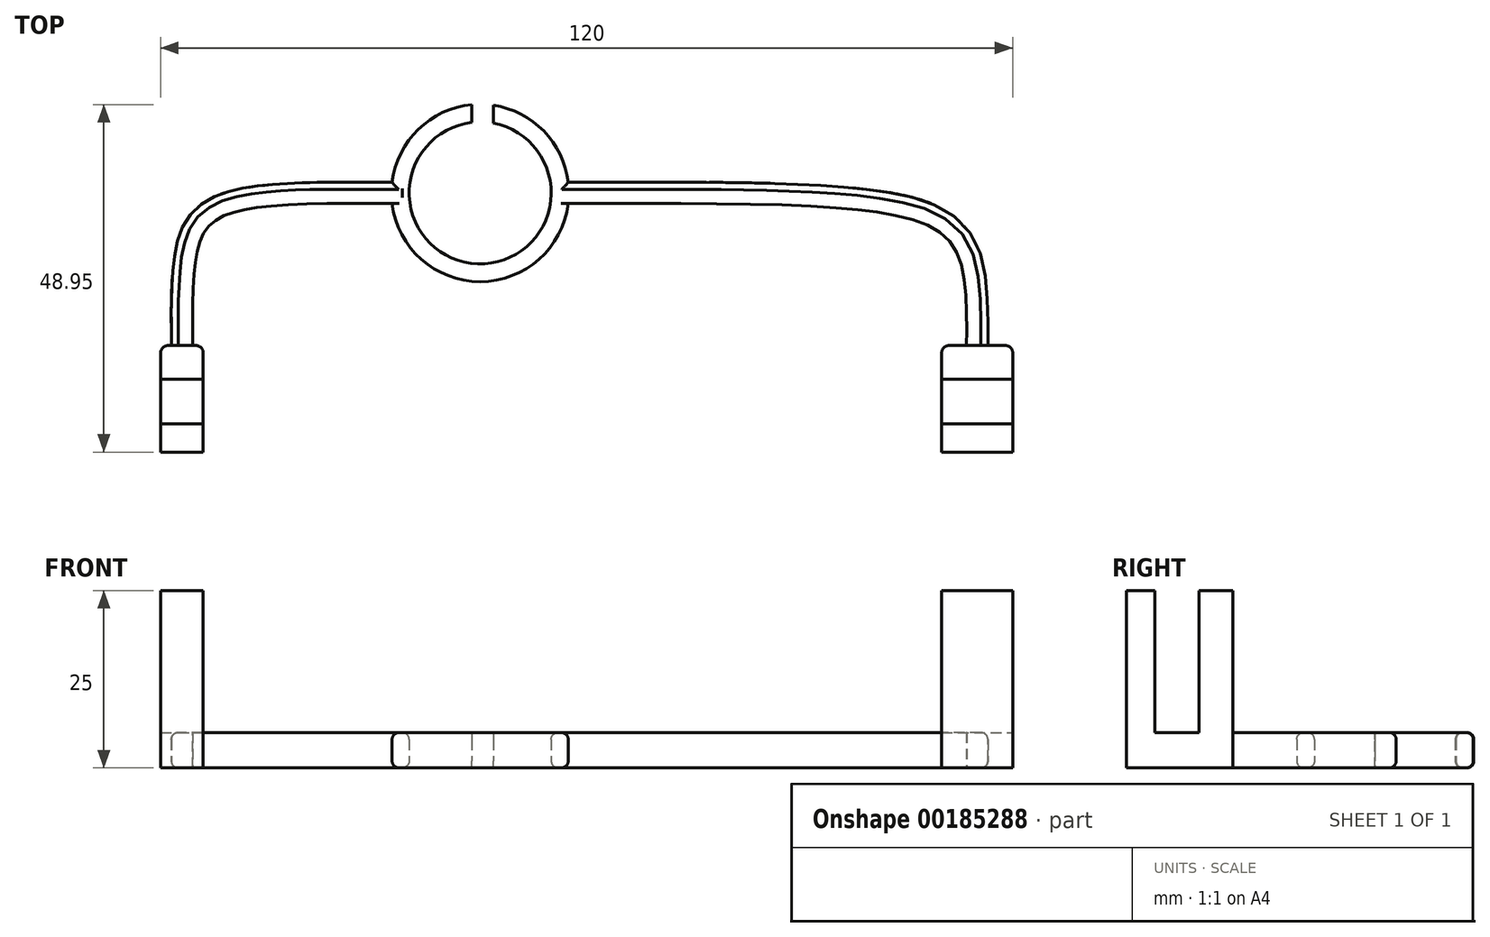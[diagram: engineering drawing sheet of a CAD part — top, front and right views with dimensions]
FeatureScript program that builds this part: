
annotation { "Feature Type Name" : "Feature", "Feature Type Description" : "" }
export const myFeature = defineFeature(function(context is Context, id is Id, definition is map)
    precondition{}
    {
        {
            var Q0;
            Q0=qCreatedBy(makeId("Top.planeOp"),FACE);
            var sketch = newSketch(context, id + "F0", { "sketchPlane" : qUnion([Q0])});
            skCircle(sketch, "E0", {"center": v(0, 0) * mm, "radius": 10 * mm});
            skCircle(sketch, "E1", {"center": v(0, 0) * mm, "radius": 12.5 * mm});
            skSolve(sketch);
        }
        {
            var Q0;
            Q0=makeQuery(id+"F0.imprint","IMPRINT",FACE,{"disambiguationData":[TD([[makeQuery(id+"F0.imprint","IMPRINT",EDGE,{"derivedFrom":sQuery(id+"F0.wireOp",EDGE,"E0")}),-1.0]])]});
            extrude(context, id + "F1", {"entities" : qUnion([Q0]), "depth" : 5 * mm});
        }
        {
            var Q0;
            Q0=makeQuery(id+"F1.opExtrude","CAP_FACE",FACE,{"disambiguationData":[OSD([sQuery(id+"F0.wireOp",EDGE,"E0"),sQuery(id+"F0.wireOp",EDGE,"E1")])],"isStart":false});
            var Q1;
            Q1=makeQuery(id+"F1.opExtrude","CAP_FACE",FACE,{"disambiguationData":[OSD([sQuery(id+"F0.wireOp",EDGE,"E0"),sQuery(id+"F0.wireOp",EDGE,"E1")])],"isStart":true});
            fillet(context, id + "F2", {"entities" : qUnion([Q0, Q1]), "radius" : 1 * mm, "tangentPropagation" : true, "allowEdgeOverflow" : false});
        }
        {
            var Q0;
            Q0=qCreatedBy(makeId("Top.planeOp"),FACE);
            var sketch = newSketch(context, id + "F3", { "sketchPlane" : qUnion([Q0])});
            skLineSegment(sketch, "E2", {"start": v(70, 0) * mm, "end": v(0, 0) * mm, "construction": true});
            skLineSegment(sketch, "E3", {"start": v(70, 0) * mm, "end": v(70, -29) * mm, "construction": true});
            skLineSegment(sketch, "E4.bottom", {"start": v(75, -36.5) * mm, "end": v(65, -36.5) * mm});
            skLineSegment(sketch, "E4.top", {"start": v(75, -21.5) * mm, "end": v(65, -21.5) * mm});
            skLineSegment(sketch, "E4.left", {"start": v(75, -36.5) * mm, "end": v(75, -21.5) * mm});
            skLineSegment(sketch, "E4.right", {"start": v(65, -36.5) * mm, "end": v(65, -21.5) * mm});
            skPoint(sketch, "E4.middle", {"position": v(70, -29) * mm});
            skFitSpline(sketch, "E5", {"points": [v(11.07, 0) * mm, v(70, -21.5) * mm], "startDerivative": vector(176.8, 0) * mm, "endDerivative": vector(0, -64.5) * mm});
            skLineSegment(sketch, "E6", {"start": v(0, 0) * mm, "end": v(-42, 0) * mm, "construction": true});
            skLineSegment(sketch, "E7", {"start": v(-42, 0) * mm, "end": v(-42, -29) * mm, "construction": true});
            skLineSegment(sketch, "E8.bottom", {"start": v(-39, -36.5) * mm, "end": v(-45, -36.5) * mm});
            skLineSegment(sketch, "E8.top", {"start": v(-39, -21.5) * mm, "end": v(-45, -21.5) * mm});
            skLineSegment(sketch, "E8.left", {"start": v(-39, -36.5) * mm, "end": v(-39, -21.5) * mm});
            skLineSegment(sketch, "E8.right", {"start": v(-45, -36.5) * mm, "end": v(-45, -21.5) * mm});
            skPoint(sketch, "E8.middle", {"position": v(-42, -29) * mm});
            skSolve(sketch);
        }
        {
            var Q0;
            Q0 = qSketchRegion(id + "F3", true);
            extrude(context, id + "F4", {"entities" : qUnion([Q0]), "depth" : 25 * mm});
        }
        {
            var Q0;
            Q0=makeQuery(id+"F4.opExtrude","CAP_FACE",FACE,{"disambiguationData":[OSD([sQuery(id+"F3.wireOp",EDGE,"E4.bottom"),sQuery(id+"F3.wireOp",EDGE,"E4.top"),sQuery(id+"F3.wireOp",EDGE,"E4.left"),sQuery(id+"F3.wireOp",EDGE,"E4.right")])],"isStart":false});
            var sketch = newSketch(context, id + "F5", { "sketchPlane" : qUnion([Q0])});
            skLineSegment(sketch, "E9.bottom", {"start": v(65, -21.5) * mm, "end": v(75, -21.5) * mm});
            skLineSegment(sketch, "E9.top", {"start": v(65, -26.25) * mm, "end": v(75, -26.25) * mm});
            skLineSegment(sketch, "E9.left", {"start": v(65, -21.5) * mm, "end": v(65, -26.25) * mm});
            skLineSegment(sketch, "E9.right", {"start": v(75, -21.5) * mm, "end": v(75, -26.25) * mm});
            skLineSegment(sketch, "E10.bottom", {"start": v(65, -36.5) * mm, "end": v(75, -36.5) * mm});
            skLineSegment(sketch, "E10.top", {"start": v(65, -32.5) * mm, "end": v(75, -32.5) * mm});
            skLineSegment(sketch, "E10.left", {"start": v(65, -36.5) * mm, "end": v(65, -32.5) * mm});
            skLineSegment(sketch, "E10.right", {"start": v(75, -36.5) * mm, "end": v(75, -32.5) * mm});
            skLineSegment(sketch, "E11.left", {"start": v(65, -26.25) * mm, "end": v(65, -32.5) * mm});
            skLineSegment(sketch, "E11.right", {"start": v(75, -26.25) * mm, "end": v(75, -32.5) * mm});
            skSolve(sketch);
        }
        {
            var Q0;
            Q0=makeQuery(id+"F5.imprint","IMPRINT",FACE,{"disambiguationData":[TD([[makeQuery(id+"F5.imprint","IMPRINT",EDGE,{"derivedFrom":sQuery(id+"F5.wireOp",EDGE,"E9.top")}),-1.0]])]});
            extrude(context, id + "F6", {"entities" : qUnion([Q0]), "operationType" : NewBodyOperationType.REMOVE, "oppositeDirection" : true, "depth" : 20 * mm});
        }
        {
            var Q0;
            Q0=qCreatedBy(makeId("Top.planeOp"),FACE);
            var sketch = newSketch(context, id + "F7", { "sketchPlane" : qUnion([Q0])});
            skFitSpline(sketch, "E12.0", {"points": [v(11.02, -1.5) * mm, v(18.4, -1.5) * mm, v(31.32, -1.5) * mm, v(43.4, -1.72) * mm, v(50.95, -2.17) * mm, v(55.62, -2.67) * mm, v(59.38, -3.35) * mm, v(62.29, -4.24) * mm, v(64.43, -5.32) * mm, v(65.93, -6.59) * mm, v(67, -8.1) * mm, v(67.74, -10.02) * mm, v(68.2, -12.44) * mm, v(68.45, -15.38) * mm, v(68.52, -18.86) * mm, v(68.5, -21.55) * mm, v(68.5, -22.98) * mm]});
            skFitSpline(sketch, "E13.0", {"points": [v(11.02, 1.5) * mm, v(18.4, 1.5) * mm, v(31.33, 1.5) * mm, v(43.49, 1.27) * mm, v(51.17, 0.82) * mm, v(56.02, 0.3) * mm, v(60.04, -0.42) * mm, v(63.35, -1.42) * mm, v(66.05, -2.76) * mm, v(68.17, -4.53) * mm, v(69.69, -6.72) * mm, v(70.65, -9.25) * mm, v(71.2, -12.08) * mm, v(71.44, -15.27) * mm, v(71.51, -18.86) * mm, v(71.5, -21.57) * mm, v(71.5, -23) * mm]});
            skLineSegment(sketch, "E14", {"start": v(11.02, 1.5) * mm, "end": v(11.02, -1.5) * mm});
            skLineSegment(sketch, "E15", {"start": v(68.5, -22.98) * mm, "end": v(71.5, -23) * mm});
            skSolve(sketch);
        }
        {
            var Q0;
            Q0=makeQuery(id+"F7.imprint","IMPRINT",FACE,{"disambiguationData":[TD([[makeQuery(id+"F7.imprint","IMPRINT",EDGE,{"derivedFrom":sQuery(id+"F7.wireOp",EDGE,"E12.0")}),1.0]])]});
            extrude(context, id + "F8", {"entities" : qUnion([Q0]), "operationType" : NewBodyOperationType.ADD, "depth" : 5 * mm});
        }
        {
            var Q0;
            Q0=qCreatedBy(makeId("Top.planeOp"),FACE);
            var sketch = newSketch(context, id + "F9", { "sketchPlane" : qUnion([Q0])});
            skFitSpline(sketch, "E16.0", {"points": [v(-10.98, 1.5) * mm, v(-14.86, 1.5) * mm, v(-21.65, 1.5) * mm, v(-28.08, 1.29) * mm, v(-32.2, 0.86) * mm, v(-34.85, 0.36) * mm, v(-37.1, -0.37) * mm, v(-39.03, -1.4) * mm, v(-40.6, -2.78) * mm, v(-41.75, -4.51) * mm, v(-42.53, -6.51) * mm, v(-43.03, -8.78) * mm, v(-43.31, -11.36) * mm, v(-43.5, -15.27) * mm, v(-43.5, -18.81) * mm, v(-43.5, -21.5) * mm]});
            skFitSpline(sketch, "E17.0", {"points": [v(-10.98, -1.5) * mm, v(-14.86, -1.5) * mm, v(-21.63, -1.5) * mm, v(-27.92, -1.7) * mm, v(-31.8, -2.12) * mm, v(-34.14, -2.56) * mm, v(-35.97, -3.16) * mm, v(-37.32, -3.9) * mm, v(-38.3, -4.78) * mm, v(-39.05, -5.88) * mm, v(-39.64, -7.34) * mm, v(-40.05, -9.23) * mm, v(-40.32, -11.57) * mm, v(-40.5, -15.3) * mm, v(-40.5, -18.81) * mm, v(-40.5, -21.5) * mm]});
            skLineSegment(sketch, "E18", {"start": v(-10.98, 1.5) * mm, "end": v(-10.98, -1.5) * mm});
            skLineSegment(sketch, "E19", {"start": v(-43.5, -21.5) * mm, "end": v(-40.5, -21.5) * mm});
            skSolve(sketch);
        }
        {
            var Q0;
            Q0 = qSketchRegion(id + "F9", true);
            extrude(context, id + "F10", {"entities" : qUnion([Q0]), "operationType" : NewBodyOperationType.ADD, "depth" : 5 * mm});
        }
        {
            var Q0;
            Q0=makeQuery(id+"F4.opExtrude","CAP_FACE",FACE,{"disambiguationData":[OSD([sQuery(id+"F3.wireOp",EDGE,"E8.bottom"),sQuery(id+"F3.wireOp",EDGE,"E8.top"),sQuery(id+"F3.wireOp",EDGE,"E8.left"),sQuery(id+"F3.wireOp",EDGE,"E8.right")])],"isStart":false});
            var sketch = newSketch(context, id + "F11", { "sketchPlane" : qUnion([Q0])});
            skLineSegment(sketch, "E20.bottom", {"start": v(-45, -21.5) * mm, "end": v(-39, -21.5) * mm});
            skLineSegment(sketch, "E20.top", {"start": v(-45, -26.25) * mm, "end": v(-39, -26.25) * mm});
            skLineSegment(sketch, "E20.left", {"start": v(-45, -21.5) * mm, "end": v(-45, -26.25) * mm});
            skLineSegment(sketch, "E20.right", {"start": v(-39, -21.5) * mm, "end": v(-39, -26.25) * mm});
            skLineSegment(sketch, "E21.bottom", {"start": v(-45, -36.5) * mm, "end": v(-39, -36.5) * mm});
            skLineSegment(sketch, "E21.top", {"start": v(-45, -32.5) * mm, "end": v(-39, -32.5) * mm});
            skLineSegment(sketch, "E21.left", {"start": v(-45, -36.5) * mm, "end": v(-45, -32.5) * mm});
            skLineSegment(sketch, "E21.right", {"start": v(-39, -36.5) * mm, "end": v(-39, -32.5) * mm});
            skLineSegment(sketch, "E22.left", {"start": v(-45, -26.25) * mm, "end": v(-45, -32.5) * mm});
            skLineSegment(sketch, "E22.right", {"start": v(-39, -26.25) * mm, "end": v(-39, -32.5) * mm});
            skSolve(sketch);
        }
        {
            var Q0;
            Q0=makeQuery(id+"F11.imprint","IMPRINT",FACE,{"disambiguationData":[TD([[makeQuery(id+"F11.imprint","IMPRINT",EDGE,{"derivedFrom":sQuery(id+"F11.wireOp",EDGE,"E20.top")}),-1.0]])]});
            extrude(context, id + "F12", {"entities" : qUnion([Q0]), "operationType" : NewBodyOperationType.REMOVE, "oppositeDirection" : true, "depth" : 20 * mm});
        }
        {
            var Q0;
            Q0=makeQuery(id+"F10.boolean.opBoolean","MERGE",FACE,{"derivedFrom":[makeQuery(id+"F8.boolean.opBoolean","MERGE",FACE,{"derivedFrom":[makeQuery(id+"F1.opExtrude","CAP_FACE",FACE,{"disambiguationData":[OSD([sQuery(id+"F0.wireOp",EDGE,"E0"),sQuery(id+"F0.wireOp",EDGE,"E1")])],"isStart":false}),makeQuery(id+"F8.opExtrude","CAP_FACE",FACE,{"disambiguationData":[OSD([sQuery(id+"F7.wireOp",EDGE,"E12.0"),sQuery(id+"F7.wireOp",EDGE,"E13.0"),sQuery(id+"F7.wireOp",EDGE,"E14"),sQuery(id+"F7.wireOp",EDGE,"E15")])],"isStart":false})]}),makeQuery(id+"F10.opExtrude","CAP_FACE",FACE,{"disambiguationData":[OSD([sQuery(id+"F9.wireOp",EDGE,"E16.0"),sQuery(id+"F9.wireOp",EDGE,"E17.0"),sQuery(id+"F9.wireOp",EDGE,"E18"),sQuery(id+"F9.wireOp",EDGE,"E19")])],"isStart":false})]});
            var sketch = newSketch(context, id + "F13", { "sketchPlane" : qUnion([Q0])});
            skLineSegment(sketch, "E23.bottom", {"start": v(-1.16, 13.9) * mm, "end": v(1.84, 13.9) * mm});
            skLineSegment(sketch, "E23.top", {"start": v(-1.16, 8.9) * mm, "end": v(1.84, 8.9) * mm});
            skLineSegment(sketch, "E23.left", {"start": v(-1.16, 13.9) * mm, "end": v(-1.16, 8.9) * mm});
            skLineSegment(sketch, "E23.right", {"start": v(1.84, 13.9) * mm, "end": v(1.84, 8.9) * mm});
            skSolve(sketch);
        }
        {
            var Q0;
            Q0 = qSketchRegion(id + "F13", true);
            extrude(context, id + "F14", {"entities" : qUnion([Q0]), "operationType" : NewBodyOperationType.REMOVE, "oppositeDirection" : true, "depth" : 5 * mm});
        }
        {
            var Q0;
            Q0=makeQuery(id+"F4.opExtrude","SWEPT_EDGE",EDGE,{"disambiguationData":[OSD([sQuery(id+"F3.wireOp",EDGE,"E8.top"),sQuery(id+"F3.wireOp",EDGE,"E8.right")])]});
            var Q1;
            Q1=makeQuery(id+"F4.opExtrude","SWEPT_EDGE",EDGE,{"disambiguationData":[OSD([sQuery(id+"F3.wireOp",EDGE,"E4.top"),sQuery(id+"F3.wireOp",EDGE,"E4.left")])]});
            var Q2;
            Q2=makeQuery(id+"F4.opExtrude","SWEPT_EDGE",EDGE,{"disambiguationData":[OSD([sQuery(id+"F3.wireOp",EDGE,"E4.top"),sQuery(id+"F3.wireOp",EDGE,"E4.right")])]});
            var Q3;
            Q3=makeQuery(id+"F4.opExtrude","SWEPT_EDGE",EDGE,{"disambiguationData":[OSD([sQuery(id+"F3.wireOp",EDGE,"E8.top"),sQuery(id+"F3.wireOp",EDGE,"E8.left")])]});
            fillet(context, id + "F15", {"entities" : qUnion([Q0, Q1, Q2, Q3]), "radius" : 1 * mm, "tangentPropagation" : true, "allowEdgeOverflow" : false});
        }
        {
            var Q0;
            Q0=makeQuery(id+"F8.opExtrude","CAP_EDGE",EDGE,{"disambiguationData":[OSD([sQuery(id+"F7.wireOp",EDGE,"E13.0")])],"isStart":false});
            var Q1;
            Q1=makeQuery(id+"F10.opExtrude","CAP_EDGE",EDGE,{"disambiguationData":[OSD([sQuery(id+"F9.wireOp",EDGE,"E16.0")])],"isStart":false});
            fillet(context, id + "F16", {"entities" : qUnion([Q0, Q1]), "radius" : 1 * mm, "tangentPropagation" : true, "allowEdgeOverflow" : false});
        }
        {
            var Q0;
            Q0=makeQuery(id+"F8.opExtrude","CAP_EDGE",EDGE,{"disambiguationData":[OSD([sQuery(id+"F7.wireOp",EDGE,"E13.0")])],"isStart":true});
            var Q1;
            Q1=makeQuery(id+"F10.opExtrude","CAP_EDGE",EDGE,{"disambiguationData":[OSD([sQuery(id+"F9.wireOp",EDGE,"E16.0")])],"isStart":true});
            fillet(context, id + "F17", {"entities" : qUnion([Q0, Q1]), "radius" : 1 * mm, "tangentPropagation" : true, "allowEdgeOverflow" : false});
        }
    });
